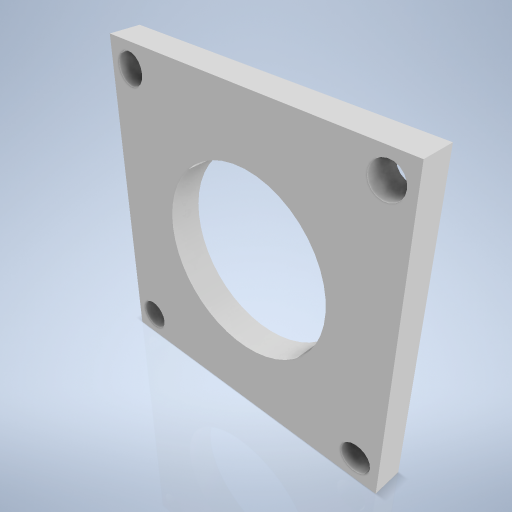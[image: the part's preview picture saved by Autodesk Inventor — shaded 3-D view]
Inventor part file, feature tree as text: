
AUTODESK INVENTOR PART (.ipt)
format: ipt  version: 2024.2 (Build 282272000, 272)  size: 244,736 bytes
history: native  units: mm
features: sketch x3, hole x2, extrude x1
ambient origin geometry x8: Origin, YZ Plane, XZ Plane, XY Plane, X Axis, Y Axis, Z Axis, Center Point
bodies: Volumenkörper1 (feature_tree)
feature tree (6):
  extrude  "Extrusion1"  Depth=50.0mm
  hole  "Bohrung1"  [1 undecoded]
  hole  "Bohrung2"  [1 undecoded]
  sketch  "Skizze1"  dims[d0=50.0mm d1=50.0mm]
  sketch  "Skizze2"  dims[d2=5.0mm d3=0.0mm]
  sketch  "Skizze3"  dims[d4=29.0mm d5=6.0mm d6=4.0mm d7=2.0mm d8=90.0deg d9=8.0mm d10=20.594885mm d11=5.0mm d12=6.0mm d13=4.0mm d14=2.0mm d15=90.0deg d16=8.0mm d17=20.594885mm d18=42.248mm d19=42.248mm]
note: 2 required parameter values undecoded (feature->parameter linkage not recoverable at this tier; creation-order binding heuristic only, values carry confidence <= 0.55)
